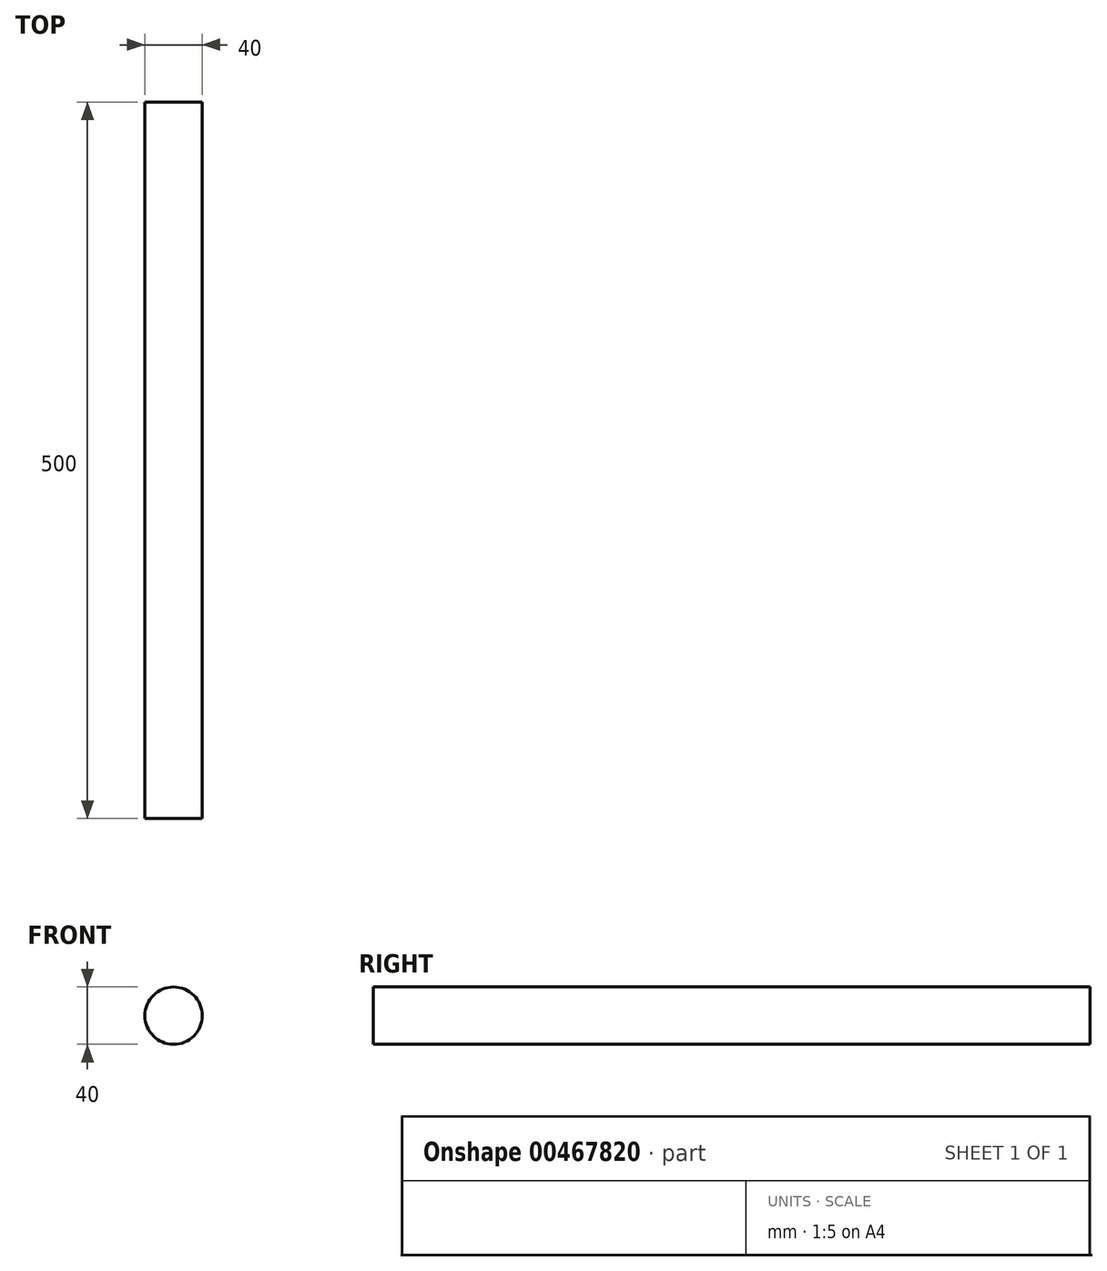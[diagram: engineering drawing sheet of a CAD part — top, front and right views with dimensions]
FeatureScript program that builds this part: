
annotation { "Feature Type Name" : "Feature", "Feature Type Description" : "" }
export const myFeature = defineFeature(function(context is Context, id is Id, definition is map)
    precondition{}
    {
        {
            var Q0;
            Q0=qCreatedBy(makeId("Front.planeOp"),FACE);
            var sketch = newSketch(context, id + "F0", { "sketchPlane" : qUnion([Q0])});
            skCircle(sketch, "E0", {"center": v(21.34, 16.24) * mm, "radius": 20 * mm});
            skSolve(sketch);
        }
        {
            var Q0;
            Q0=makeQuery(id+"F0.imprint","IMPRINT",FACE,{"disambiguationData":[TD([[makeQuery(id+"F0.imprint","IMPRINT",EDGE,{"derivedFrom":sQuery(id+"F0.wireOp",EDGE,"E0")}),1.0]])]});
            extrude(context, id + "F1", {"entities" : qUnion([Q0]), "depth" : 500 * mm});
        }
    });
